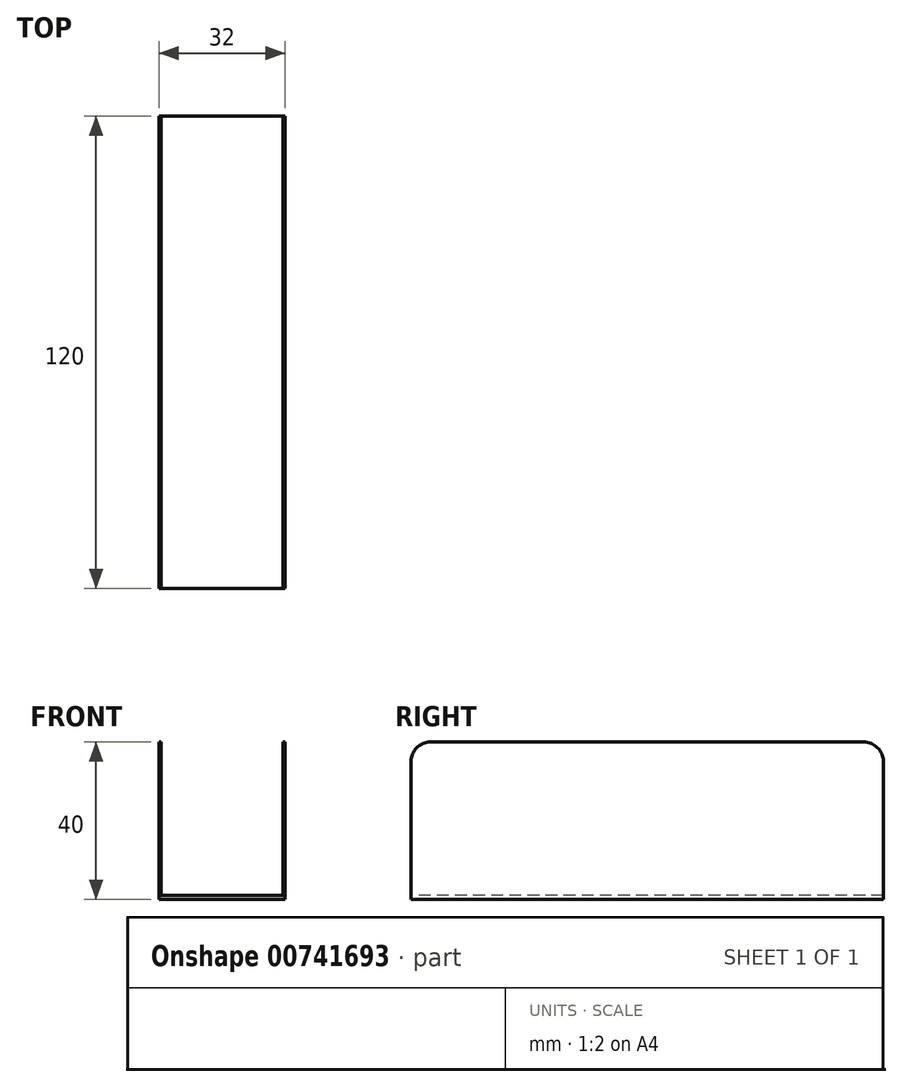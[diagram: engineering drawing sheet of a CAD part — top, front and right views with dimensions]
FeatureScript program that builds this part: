
annotation { "Feature Type Name" : "Feature", "Feature Type Description" : "" }
export const myFeature = defineFeature(function(context is Context, id is Id, definition is map)
    precondition{}
    {
        {
            var Q0;
            Q0=qCreatedBy(makeId("Front.planeOp"),FACE);
            var sketch = newSketch(context, id + "F0", { "sketchPlane" : qUnion([Q0])});
            skLineSegment(sketch, "E0.bottom", {"start": v(-52.2, 59.34) * mm, "end": v(-20.2, 59.34) * mm});
            skLineSegment(sketch, "E0.top", {"start": v(-52.2, 19.34) * mm, "end": v(-20.2, 19.34) * mm});
            skLineSegment(sketch, "E0.left", {"start": v(-52.2, 59.34) * mm, "end": v(-52.2, 19.34) * mm});
            skLineSegment(sketch, "E0.right", {"start": v(-20.2, 59.34) * mm, "end": v(-20.2, 19.34) * mm});
            skSolve(sketch);
        }
        {
            var Q0;
            Q0 = qSketchRegion(id + "F0", true);
            extrude(context, id + "F1", {"entities" : qUnion([Q0]), "depth" : 120 * mm, "offsetDistance" : 25 * mm});
        }
        {
            var Q0;
            Q0=makeQuery(id+"F1.opExtrude","CAP_FACE",FACE,{"disambiguationData":[OSD([sQuery(id+"F0.wireOp",EDGE,"E0.bottom"),sQuery(id+"F0.wireOp",EDGE,"E0.top"),sQuery(id+"F0.wireOp",EDGE,"E0.left"),sQuery(id+"F0.wireOp",EDGE,"E0.right")])],"isStart":false});
            var sketch = newSketch(context, id + "F2", { "sketchPlane" : qUnion([Q0])});
            skLineSegment(sketch, "E1.bottom", {"start": v(-51.67, 59.34) * mm, "end": v(-20.67, 59.34) * mm});
            skLineSegment(sketch, "E1.top", {"start": v(-51.67, 20.34) * mm, "end": v(-20.67, 20.34) * mm});
            skLineSegment(sketch, "E1.left", {"start": v(-51.67, 59.34) * mm, "end": v(-51.67, 20.34) * mm});
            skLineSegment(sketch, "E1.right", {"start": v(-20.67, 59.34) * mm, "end": v(-20.67, 20.34) * mm});
            skSolve(sketch);
        }
        {
            var Q0;
            Q0 = qSketchRegion(id + "F2", true);
            extrude(context, id + "F3", {"entities" : qUnion([Q0]), "operationType" : NewBodyOperationType.REMOVE, "oppositeDirection" : true, "depth" : 120 * mm, "offsetDistance" : 25 * mm});
        }
        {
            var Q0;
            {var subQ0=sQuery(id+"F0.wireOp",EDGE,"E0.bottom");var subQ1=sQuery(id+"F0.wireOp",EDGE,"E0.right");Q0=makeQuery(id+"F3.boolean.opBoolean","SPLIT",EDGE,{"disambiguationData":[TD([makeQuery(id+"F1.opExtrude","SWEPT_FACE",FACE,{"disambiguationData":[OSD([subQ1])]})])],"derivedFrom":makeQuery(id+"F1.opExtrude","CAP_EDGE",EDGE,{"disambiguationData":[OSD([subQ0])],"isStart":false})});}
            fillet(context, id + "F4", {"entities" : qUnion([Q0]), "radius" : 5 * mm, "tangentPropagation" : true, "allowEdgeOverflow" : false});
        }
        {
            var Q0;
            {var subQ0=sQuery(id+"F0.wireOp",EDGE,"E0.bottom");var subQ1=sQuery(id+"F0.wireOp",EDGE,"E0.left");Q0=makeQuery(id+"F3.boolean.opBoolean","SPLIT",EDGE,{"disambiguationData":[TD([makeQuery(id+"F1.opExtrude","SWEPT_FACE",FACE,{"disambiguationData":[OSD([subQ1])]})])],"derivedFrom":makeQuery(id+"F1.opExtrude","CAP_EDGE",EDGE,{"disambiguationData":[OSD([subQ0])],"isStart":false})});}
            fillet(context, id + "F5", {"entities" : qUnion([Q0]), "radius" : 5 * mm, "tangentPropagation" : true, "allowEdgeOverflow" : false});
        }
        {
            var Q0;
            {var subQ0=sQuery(id+"F0.wireOp",EDGE,"E0.bottom");var subQ1=sQuery(id+"F0.wireOp",EDGE,"E0.right");Q0=makeQuery(id+"F3.boolean.opBoolean","SPLIT",EDGE,{"disambiguationData":[TD([makeQuery(id+"F1.opExtrude","SWEPT_FACE",FACE,{"disambiguationData":[OSD([subQ1])]})])],"derivedFrom":makeQuery(id+"F1.opExtrude","CAP_EDGE",EDGE,{"disambiguationData":[OSD([subQ0])],"isStart":true})});}
            fillet(context, id + "F6", {"entities" : qUnion([Q0]), "radius" : 5 * mm, "tangentPropagation" : true, "allowEdgeOverflow" : false});
        }
        {
            var Q0;
            {var subQ0=sQuery(id+"F0.wireOp",EDGE,"E0.bottom");var subQ1=sQuery(id+"F0.wireOp",EDGE,"E0.left");Q0=makeQuery(id+"F3.boolean.opBoolean","SPLIT",EDGE,{"disambiguationData":[TD([makeQuery(id+"F1.opExtrude","SWEPT_FACE",FACE,{"disambiguationData":[OSD([subQ1])]})])],"derivedFrom":makeQuery(id+"F1.opExtrude","CAP_EDGE",EDGE,{"disambiguationData":[OSD([subQ0])],"isStart":true})});}
            fillet(context, id + "F7", {"entities" : qUnion([Q0]), "radius" : 5 * mm, "tangentPropagation" : true, "allowEdgeOverflow" : false});
        }
    });
